# Revit family: Storage-Teknion-CWSD_Credenza_Drawer_and_Closed_Cabinet-R2020
name_source: partatom
category: Furniture
units: mm (PartAtom-declared; Revit-internal decimal feet)

## family parameters
Always vertical = Yes
Cut with Voids When Loaded = No
OmniClass Number = 23.40.20.00
OmniClass Title = General Furniture and Specialties
Room Calculation Point = No
Shared = Yes
Work Plane-Based = No

## types (4) — shared parameters
Assembly Code = E2020200
Case, Back & Front Finish = Laminate - Teknion - RV - Very White
Manufacturer = Teknion
Manufacturer Fax = 416.661.4586
Model = CWSD____
Part Number = CWSD
Product Documentation Link = https://assets.teknion.com
Product Line = C+D
Product Page URL = https://www.teknion.com
Pull Finish = Paint - Teknion - Mica - Graphite
Series = Custom Wood
Sustainability Data = https://www.teknion.com
URL = www.teknion.com
Unit Weight URL = http://www.teknion.com
Warranty = http://www.teknion.com
zero-valued in all types: Default Elevation

## per-type parameters (varying)
| type | Description | Glass Top Visibility | Solid Top Visibility | Top Finish | Top Finish Note |
| Has Veneer Top | Custom Wood Credenza, 1/2" Top, Drawer and Closed Cabinet, Has Veneer Top | No | Yes | Wood - Teknion - DV - Sierra (Horizontal Grain) | Choose a Veneer Finish below |
| Has White Solid Surface Top | Custom Wood Credenza, 1/2" Top, Drawer and Closed Cabinet, Has White Solid Surface Top | No | Yes | Wood - Teknion - MV - Solid Surface - Glacier White | Choose Glacier White below |
| Has Grey Solid Surface Top | Custom Wood Credenza, 1/2" Top, Drawer and Closed Cabinet, Has Grey Solid Surface Top | No | Yes | Wood - Teknion - MH - Silver Grey | Choose either a Silver Grey or Elegant Grey Finish below |
| Has Backpainted Glass Top | Custom Wood Credenza, 1/2" Top, Drawer and Closed Cabinet, Has Backpainted Glass Top | Yes | No | Back-painted Glass - K7 - Teknion - Very White | Choose a Backpainted Glass Finish below |

## geometry (parser evidence)
native form markers: Blend x36, Sweep x2
no freeform markers — native parametric forms only
